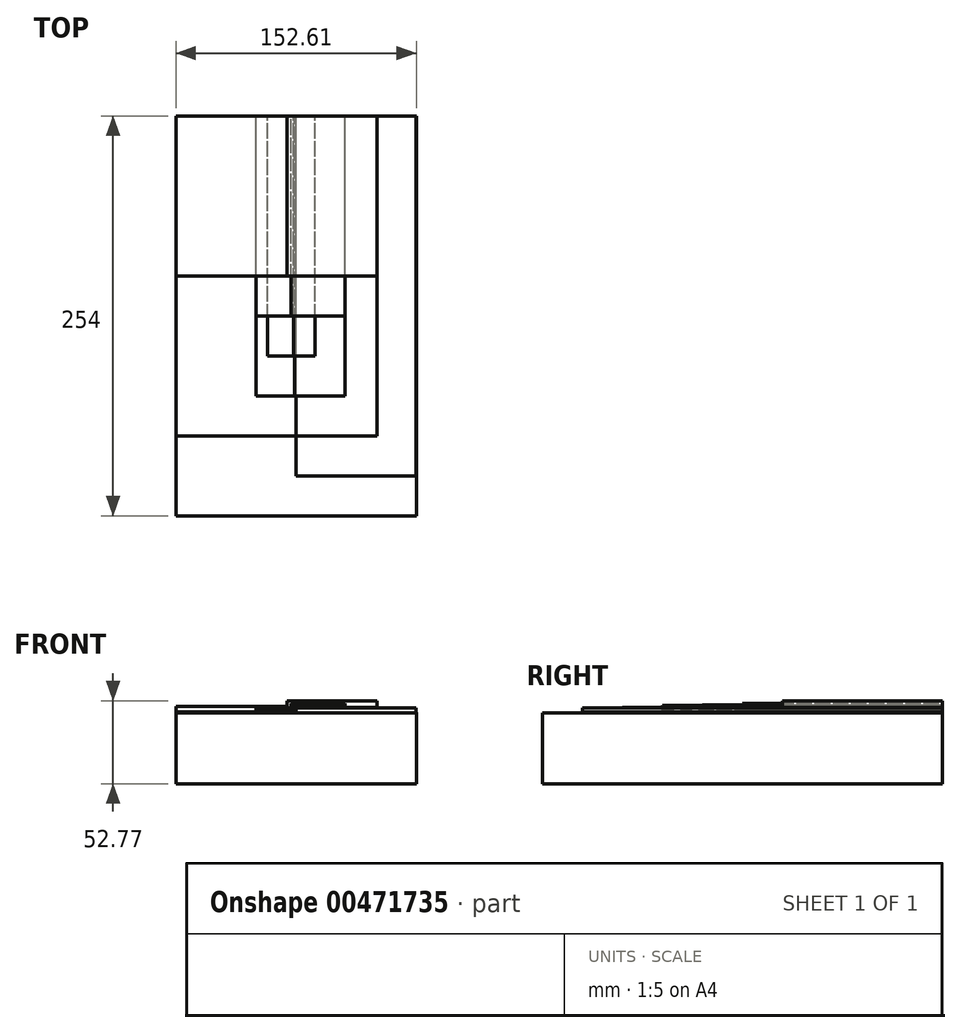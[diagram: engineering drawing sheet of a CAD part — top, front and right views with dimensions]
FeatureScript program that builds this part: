
annotation { "Feature Type Name" : "Feature", "Feature Type Description" : "" }
export const myFeature = defineFeature(function(context is Context, id is Id, definition is map)
    precondition{}
    {
        {
            var Q0;
            Q0=qCreatedBy(makeId("Front.planeOp"),FACE);
            var sketch = newSketch(context, id + "F0", { "sketchPlane" : qUnion([Q0])});
            skLineSegment(sketch, "E0.top", {"start": v(-76.44, -19.61) * mm, "end": v(76.17, -19.61) * mm});
            skLineSegment(sketch, "E0.left", {"start": v(-76.44, 25.04) * mm, "end": v(-76.44, -19.61) * mm});
            skLineSegment(sketch, "E0.right", {"start": v(76.17, 23.51) * mm, "end": v(76.17, -19.61) * mm});
            skLineSegment(sketch, "E1", {"start": v(-76.44, 25.04) * mm, "end": v(-76.44, 25.54) * mm});
            skLineSegment(sketch, "E2", {"start": v(-76.44, 25.54) * mm, "end": v(76.17, 25.54) * mm});
            skLineSegment(sketch, "E3", {"start": v(76.17, 25.54) * mm, "end": v(76.17, 23.51) * mm});
            skLineSegment(sketch, "E4", {"start": v(-76.44, 25.54) * mm, "end": v(-76.44, 26.05) * mm});
            skLineSegment(sketch, "E5", {"start": v(-76.44, 26.05) * mm, "end": v(76.04, 26.05) * mm});
            skLineSegment(sketch, "E6", {"start": v(76.04, 26.05) * mm, "end": v(76.17, 25.54) * mm});
            skLineSegment(sketch, "E7", {"start": v(-0.2, 26.05) * mm, "end": v(-0.2, 28.6) * mm});
            skLineSegment(sketch, "E8", {"start": v(-0.2, 28.6) * mm, "end": v(69.71, 28.6) * mm});
            skLineSegment(sketch, "E9", {"start": v(-0.2, 28.6) * mm, "end": v(-0.2, 29.1) * mm});
            skLineSegment(sketch, "E10", {"start": v(-0.2, 29.1) * mm, "end": v(51.34, 29.1) * mm});
            skLineSegment(sketch, "E11", {"start": v(51.34, 29.1) * mm, "end": v(51.34, 28.6) * mm});
            skLineSegment(sketch, "E12", {"start": v(-25.75, 26.05) * mm, "end": v(-25.75, 27.07) * mm});
            skLineSegment(sketch, "E13", {"start": v(-25.75, 27.07) * mm, "end": v(-1.22, 27.07) * mm});
            skLineSegment(sketch, "E14", {"start": v(-1.22, 27.07) * mm, "end": v(-1.22, 30.12) * mm});
            skLineSegment(sketch, "E15", {"start": v(-1.22, 30.12) * mm, "end": v(30.95, 30.12) * mm});
            skLineSegment(sketch, "E16", {"start": v(30.95, 30.12) * mm, "end": v(30.95, 29.1) * mm});
            skLineSegment(sketch, "E17", {"start": v(-18.44, 27.07) * mm, "end": v(-18.44, 27.58) * mm});
            skLineSegment(sketch, "E18", {"start": v(-18.44, 27.58) * mm, "end": v(-1.72, 27.58) * mm});
            skLineSegment(sketch, "E19", {"start": v(-1.72, 27.58) * mm, "end": v(-1.72, 30.62) * mm});
            skLineSegment(sketch, "E20", {"start": v(-1.72, 30.62) * mm, "end": v(12, 30.62) * mm});
            skLineSegment(sketch, "E21", {"start": v(12, 30.62) * mm, "end": v(12, 30.12) * mm});
            skLineSegment(sketch, "E22", {"start": v(-25.75, 27.07) * mm, "end": v(-25.75, 28.6) * mm});
            skLineSegment(sketch, "E23", {"start": v(-25.75, 28.6) * mm, "end": v(-3.25, 28.6) * mm});
            skLineSegment(sketch, "E24", {"start": v(-3.25, 28.6) * mm, "end": v(-3.25, 31.64) * mm});
            skLineSegment(sketch, "E25", {"start": v(-3.25, 31.64) * mm, "end": v(30.95, 31.64) * mm});
            skLineSegment(sketch, "E26", {"start": v(30.95, 31.64) * mm, "end": v(30.95, 30.12) * mm});
            skLineSegment(sketch, "E27", {"start": v(-1.22, 27.07) * mm, "end": v(-0.2, 27.07) * mm, "construction": true});
            skLineSegment(sketch, "E28", {"start": v(-1.72, 27.58) * mm, "end": v(-1.22, 27.58) * mm, "construction": true});
            skLineSegment(sketch, "E29", {"start": v(-3.25, 28.6) * mm, "end": v(-1.72, 28.6) * mm, "construction": true});
            skLineSegment(sketch, "E30", {"start": v(-76.44, 26.05) * mm, "end": v(-76.44, 29.6) * mm});
            skLineSegment(sketch, "E31", {"start": v(-76.44, 29.6) * mm, "end": v(-5.92, 29.6) * mm});
            skLineSegment(sketch, "E32", {"start": v(-5.92, 29.6) * mm, "end": v(-5.92, 33.16) * mm});
            skLineSegment(sketch, "E33", {"start": v(-5.92, 33.16) * mm, "end": v(51.3, 33.16) * mm});
            skLineSegment(sketch, "E34", {"start": v(51.3, 33.16) * mm, "end": v(51.34, 29.1) * mm});
            skLineSegment(sketch, "E35", {"start": v(-5.92, 29.6) * mm, "end": v(-5.92, 26.05) * mm, "construction": true});
            skLineSegment(sketch, "E36", {"start": v(69.71, 28.6) * mm, "end": v(76.04, 28.6) * mm});
            skLineSegment(sketch, "E37", {"start": v(76.04, 28.6) * mm, "end": v(76.04, 26.05) * mm});
            skLineSegment(sketch, "E38", {"start": v(-0.2, 26.05) * mm, "end": v(-0.2, 25.54) * mm});
            skSolve(sketch);
        }
        {
            var Q0;
            Q0=makeQuery(id+"F0.imprint","IMPRINT",FACE,{"disambiguationData":[TD([[makeQuery(id+"F0.imprint","IMPRINT",EDGE,{"derivedFrom":sQuery(id+"F0.wireOp",EDGE,"E0.top")}),1.0]])]});
            extrude(context, id + "F1", {"entities" : qUnion([Q0]), "depth" : 254 * mm});
        }
        {
            var Q0;
            {var subQ3=sQuery(id+"F0.wireOp",EDGE,"E7");Q0=makeQuery(id+"F0.imprint","IMPRINT",FACE,{"disambiguationData":[TD([[makeQuery(id+"F0.imprint","IMPRINT",EDGE,{"derivedFrom":subQ3}),-1.0]])]});}
            var Q1;
            {var subQ0=sQuery(id+"F0.wireOp",EDGE,"E6");Q1=makeQuery(id+"F0.imprint","IMPRINT",FACE,{"disambiguationData":[TD([[makeQuery(id+"F0.imprint","IMPRINT",EDGE,{"derivedFrom":subQ0}),-1.0]])]});}
            extrude(context, id + "F2", {"entities" : qUnion([Q0, Q1]), "depth" : 228.6 * mm});
        }
        {
            var Q0;
            {var subQ1=sQuery(id+"F0.wireOp",EDGE,"E4");Q0=makeQuery(id+"F0.imprint","IMPRINT",FACE,{"disambiguationData":[TD([[makeQuery(id+"F0.imprint","IMPRINT",EDGE,{"derivedFrom":subQ1}),-1.0]])]});}
            var Q1;
            {var subQ3=sQuery(id+"F0.wireOp",EDGE,"E9");Q1=makeQuery(id+"F0.imprint","IMPRINT",FACE,{"disambiguationData":[TD([[makeQuery(id+"F0.imprint","IMPRINT",EDGE,{"derivedFrom":subQ3}),-1.0]])]});}
            extrude(context, id + "F3", {"entities" : qUnion([Q0, Q1]), "depth" : 203.2 * mm});
        }
        {
            var Q0;
            {var subQ7=sQuery(id+"F0.wireOp",EDGE,"E7");Q0=makeQuery(id+"F0.imprint","IMPRINT",FACE,{"disambiguationData":[TD([[makeQuery(id+"F0.imprint","IMPRINT",EDGE,{"derivedFrom":subQ7}),1.0]])]});}
            extrude(context, id + "F4", {"entities" : qUnion([Q0]), "depth" : 177.8 * mm});
        }
        {
            var Q0;
            {var subQ1=sQuery(id+"F0.wireOp",EDGE,"E14");Q0=makeQuery(id+"F0.imprint","IMPRINT",FACE,{"disambiguationData":[TD([[makeQuery(id+"F0.imprint","IMPRINT",EDGE,{"derivedFrom":subQ1}),1.0]])]});}
            extrude(context, id + "F5", {"entities" : qUnion([Q0]), "depth" : 152.4 * mm});
        }
        {
            var Q0;
            {var subQ3=sQuery(id+"F0.wireOp",EDGE,"E17");Q0=makeQuery(id+"F0.imprint","IMPRINT",FACE,{"disambiguationData":[TD([[makeQuery(id+"F0.imprint","IMPRINT",EDGE,{"derivedFrom":subQ3}),1.0]])]});}
            extrude(context, id + "F6", {"entities" : qUnion([Q0]), "depth" : 127 * mm});
        }
        {
            var Q0;
            {var subQ2=sQuery(id+"F0.wireOp",EDGE,"E12");Q0=makeQuery(id+"F0.imprint","IMPRINT",FACE,{"disambiguationData":[TD([[makeQuery(id+"F0.imprint","IMPRINT",EDGE,{"derivedFrom":subQ2}),1.0]])]});}
            extrude(context, id + "F7", {"entities" : qUnion([Q0]), "depth" : 101.6 * mm});
        }
    });
